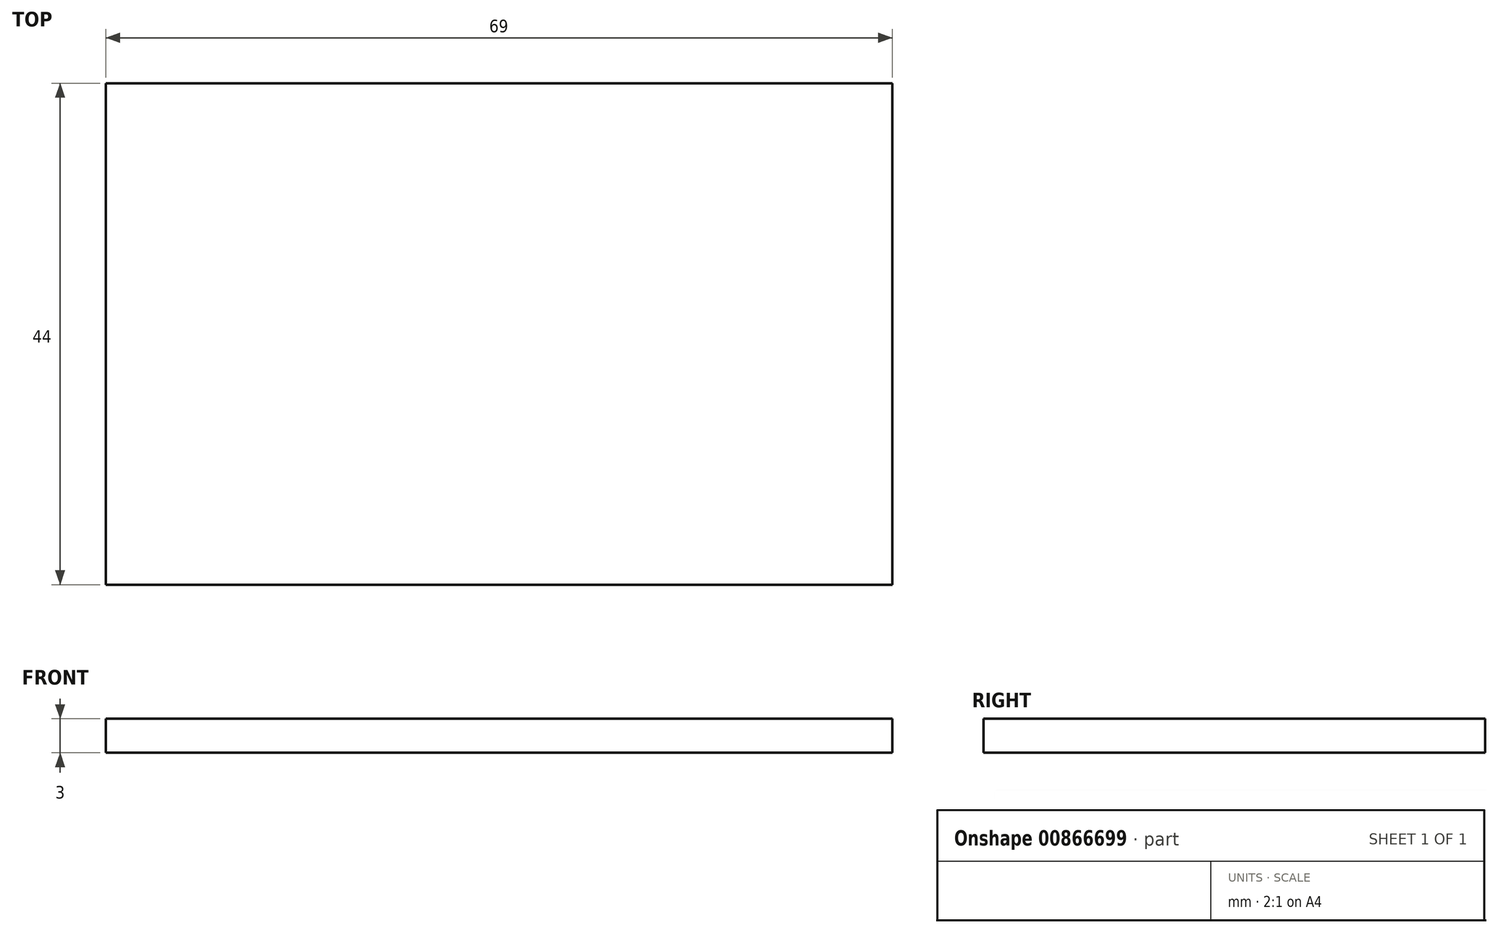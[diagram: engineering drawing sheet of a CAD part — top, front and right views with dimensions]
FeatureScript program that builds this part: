
annotation { "Feature Type Name" : "Feature", "Feature Type Description" : "" }
export const myFeature = defineFeature(function(context is Context, id is Id, definition is map)
    precondition{}
    {
        {
            var Q0;
            Q0=qCreatedBy(makeId("Top.planeOp"),FACE);
            var sketch = newSketch(context, id + "F0", { "sketchPlane" : qUnion([Q0])});
            skLineSegment(sketch, "E0.bottom", {"start": v(34.5, -22) * mm, "end": v(-34.5, -22) * mm});
            skLineSegment(sketch, "E0.top", {"start": v(34.5, 22) * mm, "end": v(-34.5, 22) * mm});
            skLineSegment(sketch, "E0.left", {"start": v(34.5, -22) * mm, "end": v(34.5, 22) * mm});
            skLineSegment(sketch, "E0.right", {"start": v(-34.5, -22) * mm, "end": v(-34.5, 22) * mm});
            skPoint(sketch, "E0.middle", {"position": v(0, 0) * mm});
            skSolve(sketch);
        }
        {
            var Q0;
            Q0=makeQuery(id+"F0.imprint","IMPRINT",FACE,{"disambiguationData":[TD([[makeQuery(id+"F0.imprint","IMPRINT",EDGE,{"derivedFrom":sQuery(id+"F0.wireOp",EDGE,"E0.bottom")}),-1.0]])]});
            extrude(context, id + "F1", {"entities" : qUnion([Q0]), "depth" : 3 * mm, "offsetDistance" : 25 * mm});
        }
    });
